# Revit family: EKF_EE_КаркасВРУ-2UnitS_IP31_PROxima
name_source: partatom
category: Электрооборудование
units: mm (PartAtom-declared; Revit-internal decimal feet)

## family parameters
Всегда вертикально = Нет
На основе рабочей плоскости = Да
Общий = Да
При загрузке вырезать с полостями = Нет
Размер круглого соединителя = Использовать диаметр
Тип детали = Силовой щит
Точка расчета площади = Нет

## types (6) — shared parameters
ADSK_Единица измерения = шт.
ADSK_Завод-изготовитель = EKF
ADSK_Количество = 1
ADSK_Марка = Каркас ВРУ-2 Unit S
ADSK_Материал = RAL 7035_Сталь
ADSK_Обозначение = Каркас ВРУ-2 Unit S
ADSK_Размер_Глубина = 450 мм
D = 9 мм
t = 1 мм
ВертПроф_Отступ = 30 мм
ДверьВерх_h = 459 мм
Изготовитель = EKF
Отступ = 20 мм
РейкаПопереч_Шаг = 759 мм
Серия номенклатуры = Unit PROxima
Степень защиты IP = -
Стойка_a = 24 мм
ТВ = EKF_2
Тип установки = -
Ц450х450 = Вл_EKF_EE_ЦокольВРУUNIT_PROxima : Цоколь к ВРУ Unit S IP31 (Вх450х450) EKF PROxima
Ц600х450 = Вл_EKF_EE_ЦокольВРУUNIT_PROxima : Цоколь к ВРУ Unit S IP31 (Вх600х450) EKF PROxima
Ц600х600 = Вл_EKF_EE_ЦокольВРУUNIT_PROxima : Цоколь к ВРУ Unit S IP31 (Вх600х600) EKF PROxima
Ц800х450 = Вл_EKF_EE_ЦокольВРУUNIT_PROxima : Цоколь к ВРУ Unit S IP31 (Вх800х450) EKF PROxima
Ц800х600 = Вл_EKF_EE_ЦокольВРУUNIT_PROxima : Цоколь к ВРУ Unit S IP31 (Вх800х600) EKF PROxima
zero-valued in all types: ADSK_Масса, Отметка по умолчанию

## per-type parameters (varying)
| type | ADSK_Код изделия | ADSK_Размер_Высота | ADSK_Размер_Ширина | ДверьНиз_h | Перемычка_L | Стойка_h | Тип | Цоколь |
| Каркас ВРУ-2 Unit S сварной IP31 (1800х450х450) EKF PROxima | mb15-10-00m | 1800 мм | 450 мм | 1310 мм | 399.6 мм | 1780 мм | 108 мм | Вл_EKF_EE_ЦокольВРУUNIT_PROxima : Цоколь к ВРУ Unit S IP31 (Вх450х450) EKF PROxima |
| Каркас ВРУ-2 Unit S сварной IP31 (1800х600х450) EKF PROxima | mb15-11-00m | 1800 мм | 600 мм | 1310 мм | 549.6 мм | 1780 мм | 109 мм | Вл_EKF_EE_ЦокольВРУUNIT_PROxima : Цоколь к ВРУ Unit S IP31 (Вх600х450) EKF PROxima |
| Каркас ВРУ-2 Unit S сварной IP31 (1800х800х450) EKF PROxima | mb15-12-00m | 1800 мм | 800 мм | 1310 мм | 749.6 мм | 1780 мм | 110 мм | Вл_EKF_EE_ЦокольВРУUNIT_PROxima : Цоколь к ВРУ Unit S IP31 (Вх800х450) EKF PROxima |
| Каркас ВРУ-2 Unit S сварной IP31 (2000х450х450) EKF PROxima | mb15-13-00m | 2000 мм | 450 мм | 1510 мм | 399.6 мм | 1980 мм | 111 мм | Вл_EKF_EE_ЦокольВРУUNIT_PROxima : Цоколь к ВРУ Unit S IP31 (Вх450х450) EKF PROxima |
| Каркас ВРУ-2 Unit S сварной IP31 (2000х600х450) EKF PROxima | mb15-14-00m | 2000 мм | 600 мм | 1510 мм | 549.6 мм | 1980 мм | 112 мм | Вл_EKF_EE_ЦокольВРУUNIT_PROxima : Цоколь к ВРУ Unit S IP31 (Вх600х450) EKF PROxima |
| Каркас ВРУ-2 Unit S сварной IP31 (2000х800х450) EKF PROxima | mb15-15-01m | 2000 мм | 800 мм | 1510 мм | 749.6 мм | 1980 мм | 113 мм | Вл_EKF_EE_ЦокольВРУUNIT_PROxima : Цоколь к ВРУ Unit S IP31 (Вх800х450) EKF PROxima |

note: column(s) folded — value = type name in every type: ADSK_Наименование
